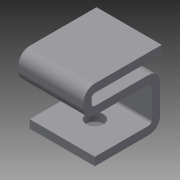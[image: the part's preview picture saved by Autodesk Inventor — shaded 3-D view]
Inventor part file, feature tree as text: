
AUTODESK INVENTOR PART (.ipt)
format: ipt  version: 2013 (Build 170138000, 138)  size: 136,192 bytes
history: native  units: in
note: dims shown in document units (in); Inventor stores cm internally (conversion verified against a paired STEP export)
features: sheet_metal_op x13, sketch x5, other x5
ambient origin geometry x8: Origin, YZ Plane, XZ Plane, XY Plane, X Axis, Y Axis, Z Axis, Center Point
bodies: Solid1 (feature_tree)
feature tree (23):
  sheet_metal_op  "Face1"
  sheet_metal_op  "Flange1"
  sheet_metal_op  "Flange2"
  sheet_metal_op  "Flange3"
  sheet_metal_op  "Flange4"
  sketch  "Sketch1"  dims[d0=1.0in]
  other  "Plate1"
  sketch  "Sketch2"  dims[d1=1.0in]
  other  "Plate2"
  sheet_metal_op  "Bend1"
  sheet_metal_op  "Corner1"
  sketch  "Sketch3"  dims[d2=0.266in]
  other  "Plate3"
  sheet_metal_op  "Bend2"
  sheet_metal_op  "Corner2"
  sketch  "Sketch4"  dims[d3=0.125in]
  other  "Plate4"
  sheet_metal_op  "Bend3"
  sheet_metal_op  "Corner3"
  sketch  "Sketch5"  dims[d4=0.125in d5=0.0625in d6=0.25in d7=0.125in d8=0.75in d9=90.0deg d10=0.05in d11=0.5in d12=0.125in d13=0.125in d14=0.125in d15=0.0625in d16=0.25in d17=0.125in d18=1.875in d19=90.0deg d20=0.05in d21=0.5in d22=0.125in d23=0.125in d24=0.125in d25=0.0625in d26=0.25in d27=0.125in d28=0.25in d29=90.0deg d30=0.05in d31=0.5in d32=0.125in d33=0.125in d34=0.125in d35=0.0625in d36=0.25in d37=0.125in d38=1.75in d39=90.0deg d40=0.05in d41=0.5in d42=0.125in d43=0.125in]
  other  "Plate5"
  sheet_metal_op  "Bend4"
  sheet_metal_op  "Corner4"
